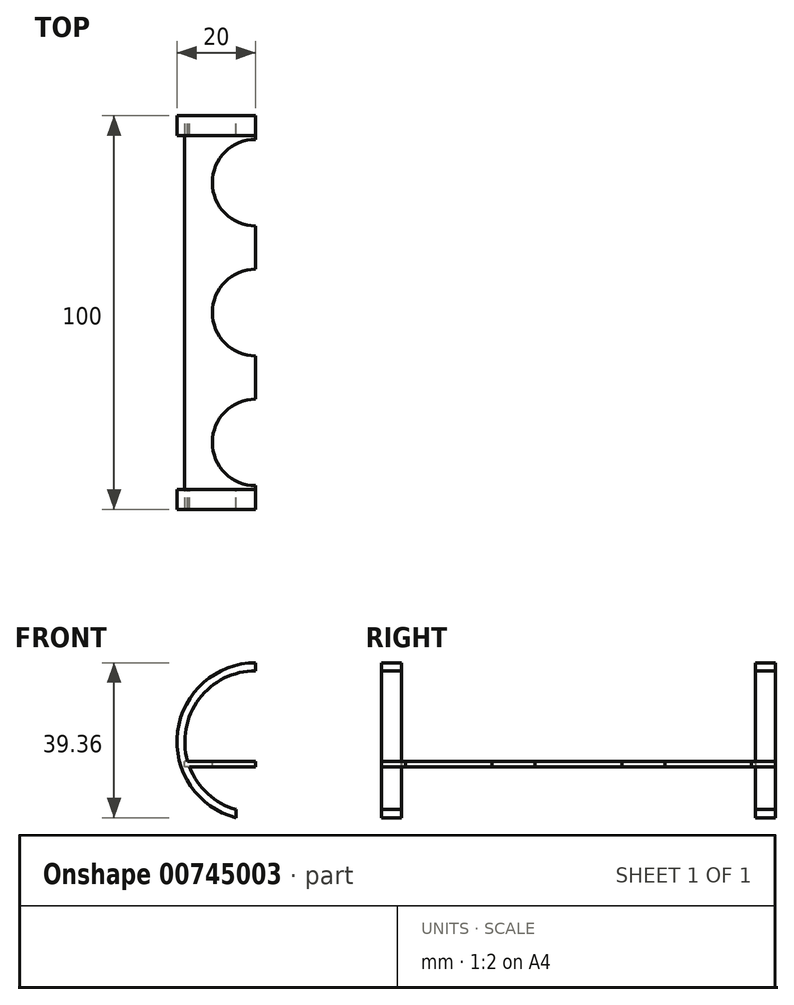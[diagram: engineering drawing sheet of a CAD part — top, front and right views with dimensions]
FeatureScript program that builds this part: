
annotation { "Feature Type Name" : "Feature", "Feature Type Description" : "" }
export const myFeature = defineFeature(function(context is Context, id is Id, definition is map)
    precondition{}
    {
        {
            var Q0;
            Q0=qCreatedBy(makeId("Front.planeOp"),FACE);
            var sketch = newSketch(context, id + "F0", { "sketchPlane" : qUnion([Q0])});
            skCircle(sketch, "E0", {"center": v(0, 0) * mm, "radius": 20 * mm});
            skCircle(sketch, "E1", {"center": v(0, 0) * mm, "radius": 18 * mm});
            skSolve(sketch);
        }
        {
            var Q0;
            Q0=makeQuery(id+"F0.imprint","IMPRINT",FACE,{"disambiguationData":[TD([[makeQuery(id+"F0.imprint","IMPRINT",EDGE,{"derivedFrom":sQuery(id+"F0.wireOp",EDGE,"E0")}),1.0]])]});
            extrude(context, id + "F1", {"entities" : qUnion([Q0]), "depth" : 5 * mm, "offsetDistance" : 25 * mm});
        }
        {
            var Q0;
            Q0=qCreatedBy(makeId("Front.planeOp"),FACE);
            var sketch = newSketch(context, id + "F2", { "sketchPlane" : qUnion([Q0])});
            skLineSegment(sketch, "E2.bottom", {"start": v(-18.06, -5) * mm, "end": v(17.94, -5) * mm});
            skLineSegment(sketch, "E2.top", {"start": v(-18.06, -6.5) * mm, "end": v(17.94, -6.5) * mm});
            skLineSegment(sketch, "E2.left", {"start": v(-18.06, -5) * mm, "end": v(-18.06, -6.5) * mm});
            skLineSegment(sketch, "E2.right", {"start": v(17.94, -5) * mm, "end": v(17.94, -6.5) * mm});
            skSolve(sketch);
        }
        {
            var Q0;
            Q0=makeQuery(id+"F2.imprint","IMPRINT",FACE,{"disambiguationData":[TD([[makeQuery(id+"F2.imprint","IMPRINT",EDGE,{"derivedFrom":sQuery(id+"F2.wireOp",EDGE,"E2.bottom")}),-1.0]])]});
            extrude(context, id + "F3", {"entities" : qUnion([Q0]), "operationType" : NewBodyOperationType.ADD, "depth" : 5 * mm, "offsetDistance" : 25 * mm, "hasSecondDirection" : true, "secondDirectionOppositeDirection" : true, "secondDirectionDepth" : 95 * mm});
        }
        {
            var Q0;
            Q0=makeQuery(id+"F3.opExtrude","CAP_FACE",FACE,{"disambiguationData":[OSD([sQuery(id+"F2.wireOp",EDGE,"E2.bottom"),sQuery(id+"F2.wireOp",EDGE,"E2.top"),sQuery(id+"F2.wireOp",EDGE,"E2.left"),sQuery(id+"F2.wireOp",EDGE,"E2.right")])],"isStart":true});
            var sketch = newSketch(context, id + "F4", { "sketchPlane" : qUnion([Q0])});
            skCircle(sketch, "E3", {"center": v(0, 0) * mm, "radius": 20 * mm});
            skCircle(sketch, "E4", {"center": v(0, 0) * mm, "radius": 18 * mm});
            skSolve(sketch);
        }
        {
            var Q0;
            Q0=makeQuery(id+"F4.imprint","IMPRINT",FACE,{"disambiguationData":[TD([[makeQuery(id+"F4.imprint","IMPRINT",EDGE,{"derivedFrom":sQuery(id+"F4.wireOp",EDGE,"E3")}),1.0]])]});
            extrude(context, id + "F5", {"entities" : qUnion([Q0]), "operationType" : NewBodyOperationType.ADD, "oppositeDirection" : true, "depth" : 5 * mm, "offsetDistance" : 25 * mm});
        }
        {
            var Q0;
            Q0=makeQuery(id+"F3.boolean.opBoolean","MERGE",FACE,{"derivedFrom":[makeQuery(id+"F1.opExtrude","CAP_FACE",FACE,{"disambiguationData":[OSD([sQuery(id+"F0.wireOp",EDGE,"E0"),sQuery(id+"F0.wireOp",EDGE,"E1")])],"isStart":false}),makeQuery(id+"F3.opExtrude","CAP_FACE",FACE,{"disambiguationData":[OSD([sQuery(id+"F2.wireOp",EDGE,"E2.bottom"),sQuery(id+"F2.wireOp",EDGE,"E2.top"),sQuery(id+"F2.wireOp",EDGE,"E2.left"),sQuery(id+"F2.wireOp",EDGE,"E2.right")])],"isStart":false})]});
            var sketch = newSketch(context, id + "F6", { "sketchPlane" : qUnion([Q0])});
            skLineSegment(sketch, "E5.bottom", {"start": v(-5, -12.52) * mm, "end": v(5, -12.52) * mm});
            skLineSegment(sketch, "E5.top", {"start": v(-5, -22.52) * mm, "end": v(5, -22.52) * mm});
            skLineSegment(sketch, "E5.left", {"start": v(-5, -12.52) * mm, "end": v(-5, -22.52) * mm});
            skLineSegment(sketch, "E5.right", {"start": v(5, -12.52) * mm, "end": v(5, -22.52) * mm});
            skSolve(sketch);
        }
        {
            var Q0;
            {var subQ0=sQuery(id+"F6.wireOp",EDGE,"E5.top");Q0=makeQuery(id+"F6.imprint","IMPRINT",FACE,{"disambiguationData":[TD([[makeQuery(id+"F6.imprint","IMPRINT",EDGE,{"derivedFrom":subQ0}),1.0]])]});}
            var Q1;
            {var subQ0=sQuery(id+"F6.wireOp",EDGE,"E5.left");var subQ1=sQuery(id+"F0.wireOp",EDGE,"E0");var subQ2=makeQuery(id+"F1.opExtrude","CAP_EDGE",EDGE,{"disambiguationData":[OSD([subQ1])],"isStart":false});var subQ3=makeQuery(id+"F6.imprint","INTERSECT",VERTEX,{"derivedFrom":[subQ2,subQ0]});Q1=makeQuery(id+"F6.imprint","IMPRINT",FACE,{"disambiguationData":[TD([[makeQuery(id+"F6.imprint","IMPRINT",EDGE,{"disambiguationData":[TD([[subQ3,-1.0]])],"derivedFrom":subQ2}),1.0]])]});}
            var Q2;
            {var subQ0=sQuery(id+"F6.wireOp",EDGE,"E5.bottom");Q2=makeQuery(id+"F6.imprint","IMPRINT",FACE,{"disambiguationData":[TD([[makeQuery(id+"F6.imprint","IMPRINT",EDGE,{"derivedFrom":subQ0}),-1.0]])]});}
            extrude(context, id + "F7", {"entities" : qUnion([Q0, Q1, Q2]), "operationType" : NewBodyOperationType.REMOVE, "endBound" : BoundingType.THROUGH_ALL, "oppositeDirection" : true, "depth" : 100 * mm, "offsetDistance" : 25 * mm});
        }
        {
            var Q0;
            Q0=makeQuery(id+"F3.opExtrude","SWEPT_FACE",FACE,{"disambiguationData":[OSD([sQuery(id+"F2.wireOp",EDGE,"E2.bottom")])]});
            var sketch = newSketch(context, id + "F8", { "sketchPlane" : qUnion([Q0])});
            skCircle(sketch, "E6", {"center": v(0, 12) * mm, "radius": 11 * mm});
            skCircle(sketch, "E7.0.1.0", {"center": v(0, 45) * mm, "radius": 11 * mm});
            skCircle(sketch, "E7.0.2.0", {"center": v(0, 78) * mm, "radius": 11 * mm});
            skLineSegment(sketch, "E7.direction1", {"start": v(0, 12) * mm, "end": v(25, 12) * mm, "construction": true});
            skLineSegment(sketch, "E7.direction2", {"start": v(0, 12) * mm, "end": v(0, 45) * mm, "construction": true});
            skSolve(sketch);
        }
        {
            var Q0;
            Q0=makeQuery(id+"F8.imprint","IMPRINT",FACE,{"disambiguationData":[TD([[makeQuery(id+"F8.imprint","IMPRINT",EDGE,{"derivedFrom":sQuery(id+"F8.wireOp",EDGE,"E6")}),1.0]])]});
            var Q1;
            Q1=makeQuery(id+"F8.imprint","IMPRINT",FACE,{"disambiguationData":[TD([[makeQuery(id+"F8.imprint","IMPRINT",EDGE,{"derivedFrom":sQuery(id+"F8.wireOp",EDGE,"E7.0.1.0")}),1.0]])]});
            var Q2;
            Q2=makeQuery(id+"F8.imprint","IMPRINT",FACE,{"disambiguationData":[TD([[makeQuery(id+"F8.imprint","IMPRINT",EDGE,{"derivedFrom":sQuery(id+"F8.wireOp",EDGE,"E7.0.2.0")}),1.0]])]});
            extrude(context, id + "F9", {"entities" : qUnion([Q0, Q1, Q2]), "operationType" : NewBodyOperationType.REMOVE, "endBound" : BoundingType.THROUGH_ALL, "oppositeDirection" : true, "depth" : 25 * mm, "offsetDistance" : 25 * mm});
        }
        {
            var Q0;
            Q0=qCreatedBy(makeId("Front.planeOp"),FACE);
            var sketch = newSketch(context, id + "F10", { "sketchPlane" : qUnion([Q0])});
            skLineSegment(sketch, "E8.bottom", {"start": v(0, 31.86) * mm, "end": v(25.25, 31.86) * mm});
            skLineSegment(sketch, "E8.top", {"start": v(0, -32.57) * mm, "end": v(25.25, -32.57) * mm});
            skLineSegment(sketch, "E8.left", {"start": v(0, 31.86) * mm, "end": v(0, -32.57) * mm});
            skLineSegment(sketch, "E8.right", {"start": v(25.25, 31.86) * mm, "end": v(25.25, -32.57) * mm});
            skSolve(sketch);
        }
        {
            var Q0;
            Q0=makeQuery(id+"F10.imprint","IMPRINT",FACE,{"disambiguationData":[TD([[makeQuery(id+"F10.imprint","IMPRINT",EDGE,{"derivedFrom":sQuery(id+"F10.wireOp",EDGE,"E8.bottom")}),-1.0]])]});
            extrude(context, id + "F11", {"entities" : qUnion([Q0]), "operationType" : NewBodyOperationType.REMOVE, "endBound" : BoundingType.SYMMETRIC, "oppositeDirection" : true, "depth" : 200 * mm, "offsetDistance" : 25 * mm});
        }
    });
